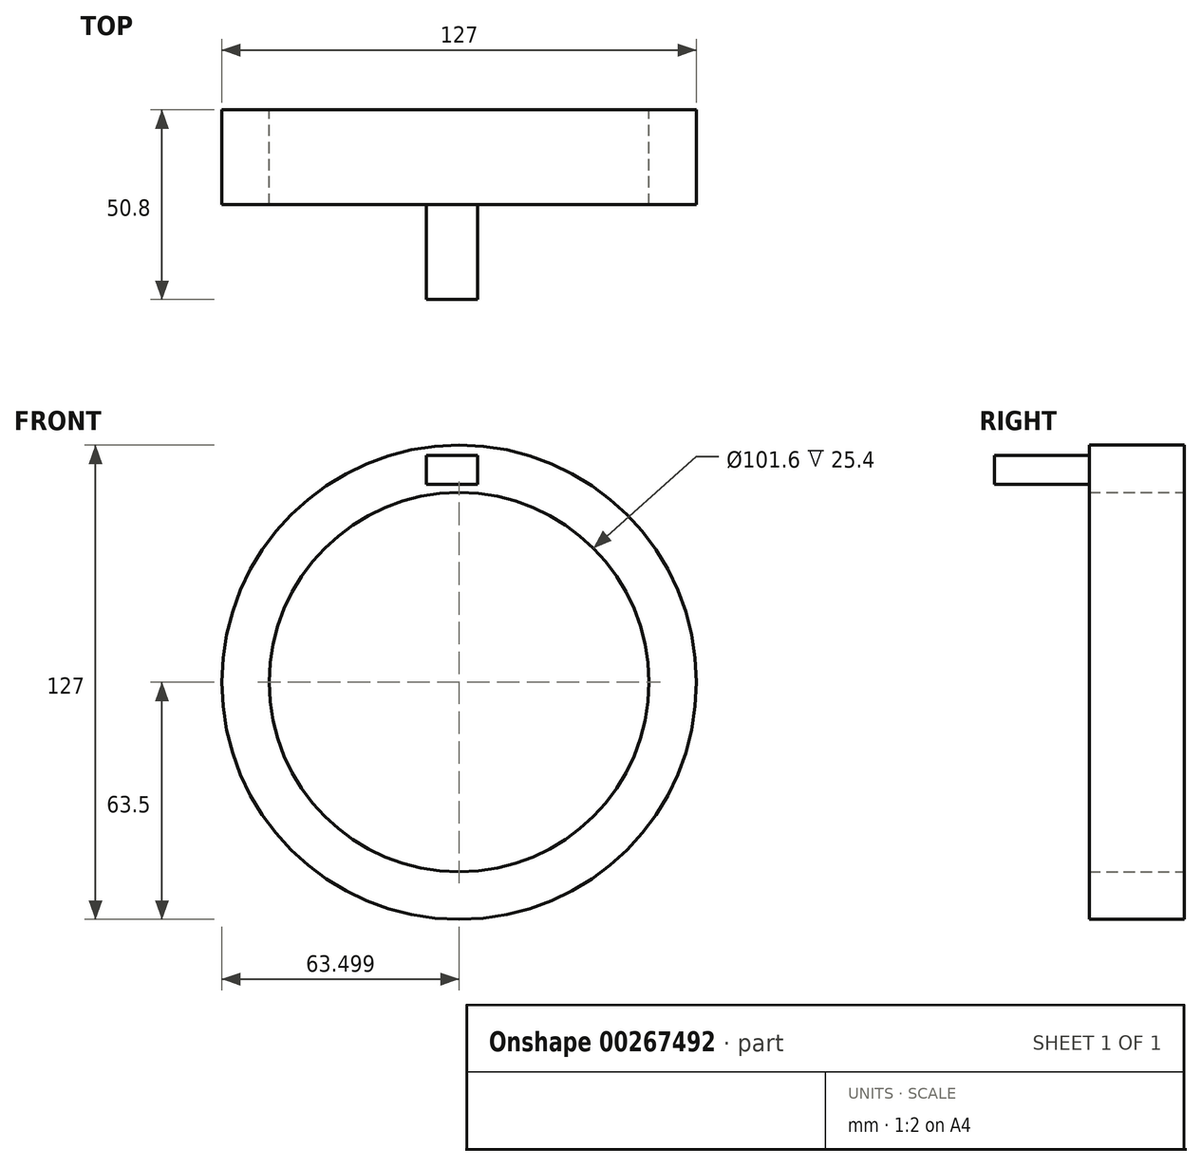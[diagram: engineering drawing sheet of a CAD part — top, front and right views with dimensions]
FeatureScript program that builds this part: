
annotation { "Feature Type Name" : "Feature", "Feature Type Description" : "" }
export const myFeature = defineFeature(function(context is Context, id is Id, definition is map)
    precondition{}
    {
        {
            var Q0;
            Q0=qCreatedBy(makeId("Front.planeOp"),FACE);
            var sketch = newSketch(context, id + "F0", { "sketchPlane" : qUnion([Q0])});
            skCircle(sketch, "E0", {"center": v(1.89, 0) * mm, "radius": 63.5 * mm});
            skCircle(sketch, "E1", {"center": v(1.89, 0) * mm, "radius": 50.8 * mm});
            skLineSegment(sketch, "E2.bottom", {"start": v(-6.86, 60.8) * mm, "end": v(6.86, 60.8) * mm});
            skLineSegment(sketch, "E2.top", {"start": v(-6.86, 52.98) * mm, "end": v(6.86, 52.98) * mm});
            skLineSegment(sketch, "E2.left", {"start": v(-6.86, 60.8) * mm, "end": v(-6.86, 52.98) * mm});
            skLineSegment(sketch, "E2.right", {"start": v(6.86, 60.8) * mm, "end": v(6.86, 52.98) * mm});
            skPoint(sketch, "E2.middle", {"position": v(0, 56.9) * mm});
            skSolve(sketch);
        }
        {
            var Q0;
            Q0=makeQuery(id+"F0.imprint","IMPRINT",FACE,{"disambiguationData":[TD([[makeQuery(id+"F0.imprint","IMPRINT",EDGE,{"derivedFrom":sQuery(id+"F0.wireOp",EDGE,"E0")}),1.0]])]});
            extrude(context, id + "F1", {"entities" : qUnion([Q0]), "depth" : 25.4 * mm});
        }
        {
            var Q0;
            Q0=makeQuery(id+"F0.imprint","IMPRINT",FACE,{"disambiguationData":[TD([[makeQuery(id+"F0.imprint","IMPRINT",EDGE,{"derivedFrom":sQuery(id+"F0.wireOp",EDGE,"E2.bottom")}),-1.0]])]});
            extrude(context, id + "F2", {"entities" : qUnion([Q0]), "operationType" : NewBodyOperationType.ADD, "depth" : 50.8 * mm});
        }
    });
